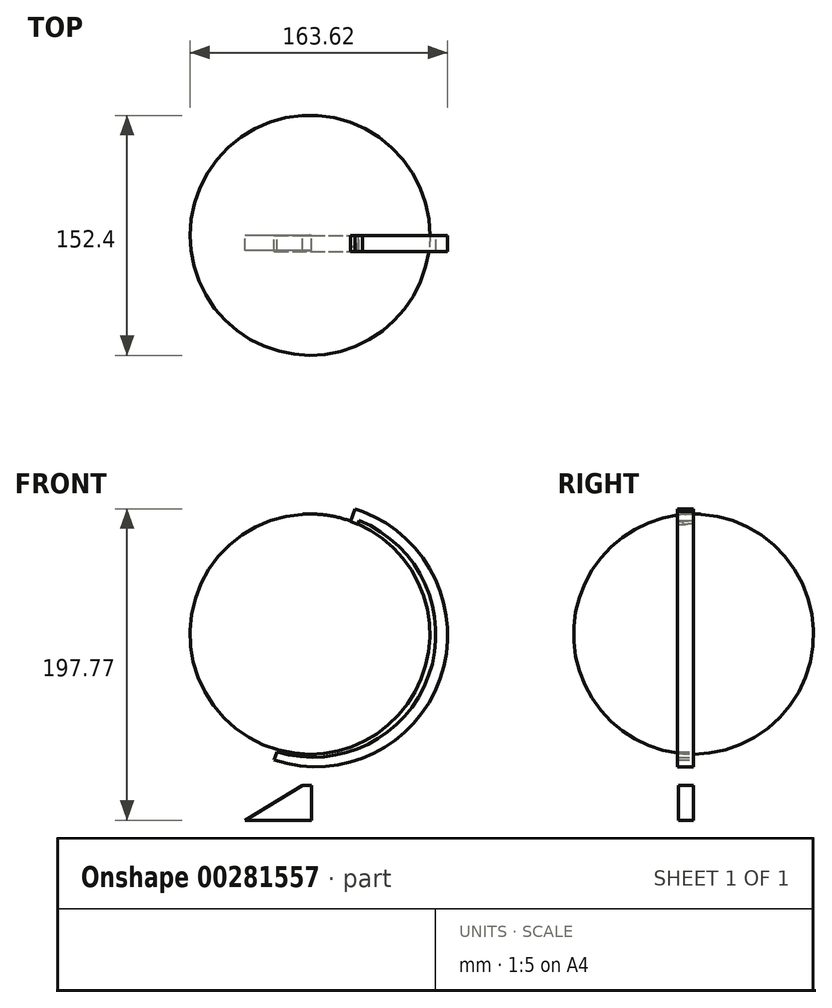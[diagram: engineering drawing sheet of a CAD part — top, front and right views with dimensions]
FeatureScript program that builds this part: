
annotation { "Feature Type Name" : "Feature", "Feature Type Description" : "" }
export const myFeature = defineFeature(function(context is Context, id is Id, definition is map)
    precondition{}
    {
        {
            var Q0;
            Q0=qCreatedBy(makeId("Front.planeOp"),FACE);
            var sketch = newSketch(context, id + "F0", { "sketchPlane" : qUnion([Q0])});
            skLineSegment(sketch, "E0", {"start": v(0, 76) * mm, "end": v(0, -76.55) * mm});
            skArc(sketch, "E1", {"start": v(0, -76.55) * mm, "mid": v(76.2, -0.27) * mm, "end": v(0, 76) * mm});
            skLineSegment(sketch, "E2", {"start": v(5.12, 75.83) * mm, "end": v(5.13, 75.83) * mm});
            skSolve(sketch);
        }
        {
            var Q0;
            Q0 = qSketchRegion(id + "F0", true);
            var Q1;
            Q1=sQuery(id+"F0.wireOp",EDGE,"E0");
            revolve(context, id + "F1", {"entities" : qUnion([Q0]), "axis" : qUnion([Q1]), "revolveType" : RevolveType.FULL});
        }
        {
            var Q0;
            Q0=qCreatedBy(makeId("Front.planeOp"),FACE);
            var sketch = newSketch(context, id + "F2", { "sketchPlane" : qUnion([Q0])});
            skArc(sketch, "E3", {"start": v(-22.66, -80.24) * mm, "mid": v(82.6, -28.73) * mm, "end": v(33.37, 77.61) * mm});
            skArc(sketch, "E4", {"start": v(-21.17, -74.96) * mm, "mid": v(75.43, -26.71) * mm, "end": v(31.3, 71.83) * mm});
            skLineSegment(sketch, "E5", {"start": v(-22.66, -80.24) * mm, "end": v(-21.17, -74.96) * mm});
            skLineSegment(sketch, "E6.0", {"start": v(-21.17, -74.96) * mm, "end": v(33.37, 77.61) * mm, "construction": true});
            skLineSegment(sketch, "E7", {"start": v(33.37, 77.61) * mm, "end": v(31.3, 71.83) * mm});
            skLineSegment(sketch, "E8", {"start": v(-22.66, -80.24) * mm, "end": v(-19.92, -71.47) * mm});
            skLineSegment(sketch, "E9", {"start": v(-22.66, -80.24) * mm, "end": v(-27.53, -78.87) * mm});
            skLineSegment(sketch, "E10", {"start": v(33.37, 77.61) * mm, "end": v(29.76, 67.51) * mm});
            skLineSegment(sketch, "E11", {"start": v(33.37, 77.61) * mm, "end": v(28.58, 79.32) * mm});
            skLineSegment(sketch, "E12", {"start": v(28.58, 79.32) * mm, "end": v(25.67, 71.16) * mm});
            skLineSegment(sketch, "E13", {"start": v(25.67, 71.16) * mm, "end": v(30.45, 69.45) * mm});
            skLineSegment(sketch, "E14", {"start": v(-27.53, -78.87) * mm, "end": v(-25.12, -71.93) * mm});
            skLineSegment(sketch, "E15", {"start": v(-25.12, -71.93) * mm, "end": v(-20.6, -73.35) * mm});
            skLineSegment(sketch, "E16", {"start": v(-20.6, -73.35) * mm, "end": v(-20.51, -73.37) * mm});
            skLineSegment(sketch, "E17", {"start": v(31.3, 71.83) * mm, "end": v(-21.17, -74.96) * mm});
            skLineSegment(sketch, "E18", {"start": v(25.67, 71.16) * mm, "end": v(-25.12, -71.93) * mm});
            skLineSegment(sketch, "E19", {"start": v(25.67, 71.16) * mm, "end": v(-25.12, -71.93) * mm, "construction": true});
            skSolve(sketch);
        }
        {
            var Q0;
            {var subQ1=sQuery(id+"F2.wireOp",EDGE,"E10");Q0=makeQuery(id+"F2.imprint","IMPRINT",FACE,{"disambiguationData":[TD([[makeQuery(id+"F2.imprint","IMPRINT",EDGE,{"derivedFrom":subQ1}),-1.0]])]});}
            var Q1;
            {var subQ0=sQuery(id+"F2.wireOp",EDGE,"E3");Q1=makeQuery(id+"F2.imprint","IMPRINT",FACE,{"disambiguationData":[TD([[makeQuery(id+"F2.imprint","IMPRINT",EDGE,{"derivedFrom":subQ0}),1.0]])]});}
            extrude(context, id + "F3", {"entities" : qUnion([Q0, Q1]), "operationType" : NewBodyOperationType.ADD, "depth" : 10.16 * mm});
        }
        {
            var Q0;
            Q0=qCreatedBy(makeId("Front.planeOp"),FACE);
            var sketch = newSketch(context, id + "F4", { "sketchPlane" : qUnion([Q0])});
            skLineSegment(sketch, "E20", {"start": v(0, -118.45) * mm, "end": v(-41.18, -118.45) * mm});
            skLineSegment(sketch, "E21", {"start": v(0.88, -96.43) * mm, "end": v(0.88, -118.45) * mm});
            skLineSegment(sketch, "E22", {"start": v(0.88, -118.45) * mm, "end": v(0, -118.45) * mm});
            skLineSegment(sketch, "E23", {"start": v(-4.84, -96.43) * mm, "end": v(-41.18, -118.45) * mm});
            skLineSegment(sketch, "E24", {"start": v(-4.84, -96.43) * mm, "end": v(0.88, -96.43) * mm});
            skSolve(sketch);
        }
        {
            var Q0;
            Q0=makeQuery(id+"F4.imprint","IMPRINT",FACE,{"disambiguationData":[TD([[makeQuery(id+"F4.imprint","IMPRINT",EDGE,{"derivedFrom":sQuery(id+"F4.wireOp",EDGE,"E21")}),1.0]])]});
            var Q1;
            Q1=makeQuery(id+"F4.imprint","IMPRINT",FACE,{"disambiguationData":[TD([[makeQuery(id+"F4.imprint","IMPRINT",EDGE,{"derivedFrom":sQuery(id+"F4.wireOp",EDGE,"E20")}),-1.0]])]});
            extrude(context, id + "F5", {"entities" : qUnion([Q0, Q1]), "operationType" : NewBodyOperationType.ADD, "depth" : 9.6 * mm});
        }
    });
